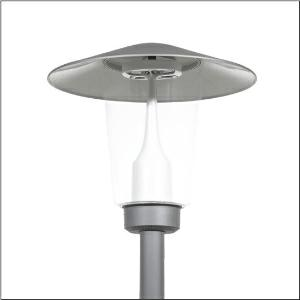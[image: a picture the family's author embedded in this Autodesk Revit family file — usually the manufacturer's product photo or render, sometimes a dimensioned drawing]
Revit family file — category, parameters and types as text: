
# Revit family: pilzleuchte_iq___st1_2a_5xa5235kf14h_dd17
name_source: partatom
category: Lighting Fixtures
units: mm (PartAtom-declared; Revit-internal decimal feet)

## family parameters
Cut with Voids When Loaded = No
Host = Face
Light Source = No
Part Type = Normal
Room Calculation Point = No
Round Connector Dimension = Use Diameter
Shared = No

## types (1)
- --- (1 x LED, 1550 lm, 10 W, 4000K)
    Apparent Load = 10 VA
    CIE Flux Codes = 24 61 93 98 100
    Color Rendering = 70
    Color Temperature = 4000K
    Default Elevation = 1800 mm
    Description = Mushroom Luminaire iQ, mast luminaire, Module 540 iQ-SR, primary light control with 3 zone facetted reflector, of plastic, silver coated, highly specular, structured, primary optical cover: cover, of PMMA, transparent, light distribution: ST1.2a, light emission: direct distribution, primary light characteristic: asymmetric, installation type: post-top, LED, High Power LED, rated luminous flux: 1.550lm, luminous efficacy: 155lm/W, light colour: 740, colour temperature: 4000K, control gear: ECG iQ, control: presetting dimming logarithmic, Street-Remote, Auto-Match, Temp-Guard, Lumen-Switch, Night-Set, Smart-Wire, Light-Fading, Desk-Remote (wireless, voltage-free reading and setting of iQ features in the workshop via application-optimized NFC function/RFID function), optimised constant luminous flux control (CLO 2.0), with terminal, 6-pole, max. 2.5mm², mains connection: 230..240V, AC, 50/60Hz, start of lifetime: 10W, end of service life: 10W, reduction: 5W, luminaire housing, upper part, of glass-fibre reinforced polyester, coated, Siteco® metallic grey (DB 702S), diameter: 650mm, height: 586mm, spigot size: d x l = 76 x 70mm (post-top) | with reducer (optional accessory) 60 x 70mm, post-top mast mounting element, of diecast aluminium, coated, Siteco® metallic grey (DB 702S), Module 540 iQ-SR, traffic white (RAL 9016), equipment: standard, protection rating (complete): IP65, insulation class (complete): insulation class II (safety insulation), certification: CE, ENEC, VDE, packaging unit: 1 piece

Light Distribution: ST1.2a
    Height = 586 mm
    Lamp = 1 x LED
    Lamp Light Flux = 1550 lm
    Lamp Power = 10 W
    Lamp count = 1
    Length = 650 mm
    Luminous efficacy = 155 lm/W
    Manufacturer = Siteco
    ModVariant = No
    Model = 5XA5235KF14H
    Number of Poles = 1
    OnlyDefault = Yes
    Power Factor = 1
    Product Name = Pilzleuchte iQ | ST1.2a
    Product group = mast luminaire | pylon top
    ProductGroupID = 6100
    Protection Class = Protection class II
    Protection Degree = IP 65
    RLX_Detail_Level = 1
    RLX_Emergency_Light_Flux = 0 lm
    RLX_Emergency_Type = 0
    RLX_Emergency_Type_DB = No
    RlxData = <blob elided: 127665 chars, md5=6ab1d33b>
    Socket = socket
    Standby Power = 0 W
    System Light Flux = 1550 lm
    System Power = 10 W
    Type Comments = factory setting: luminous flux: 100 % | dim-lin: 254 | 401 mA
    Type Image = l_1006077.jpg
    URL = http://relux.com
    VarID = @adj_110909
    Voltage = 0 V
    Weight = 0.00 kg
    Width = 0 mm  [stored 0 ft]

note: [stored X ft] marks values corroborated as IEEE doubles in the binary element streams (Revit-internal decimal feet)

## geometry (parser evidence)
native form markers: Blend x4, Sweep x13
no freeform markers — native parametric forms only
